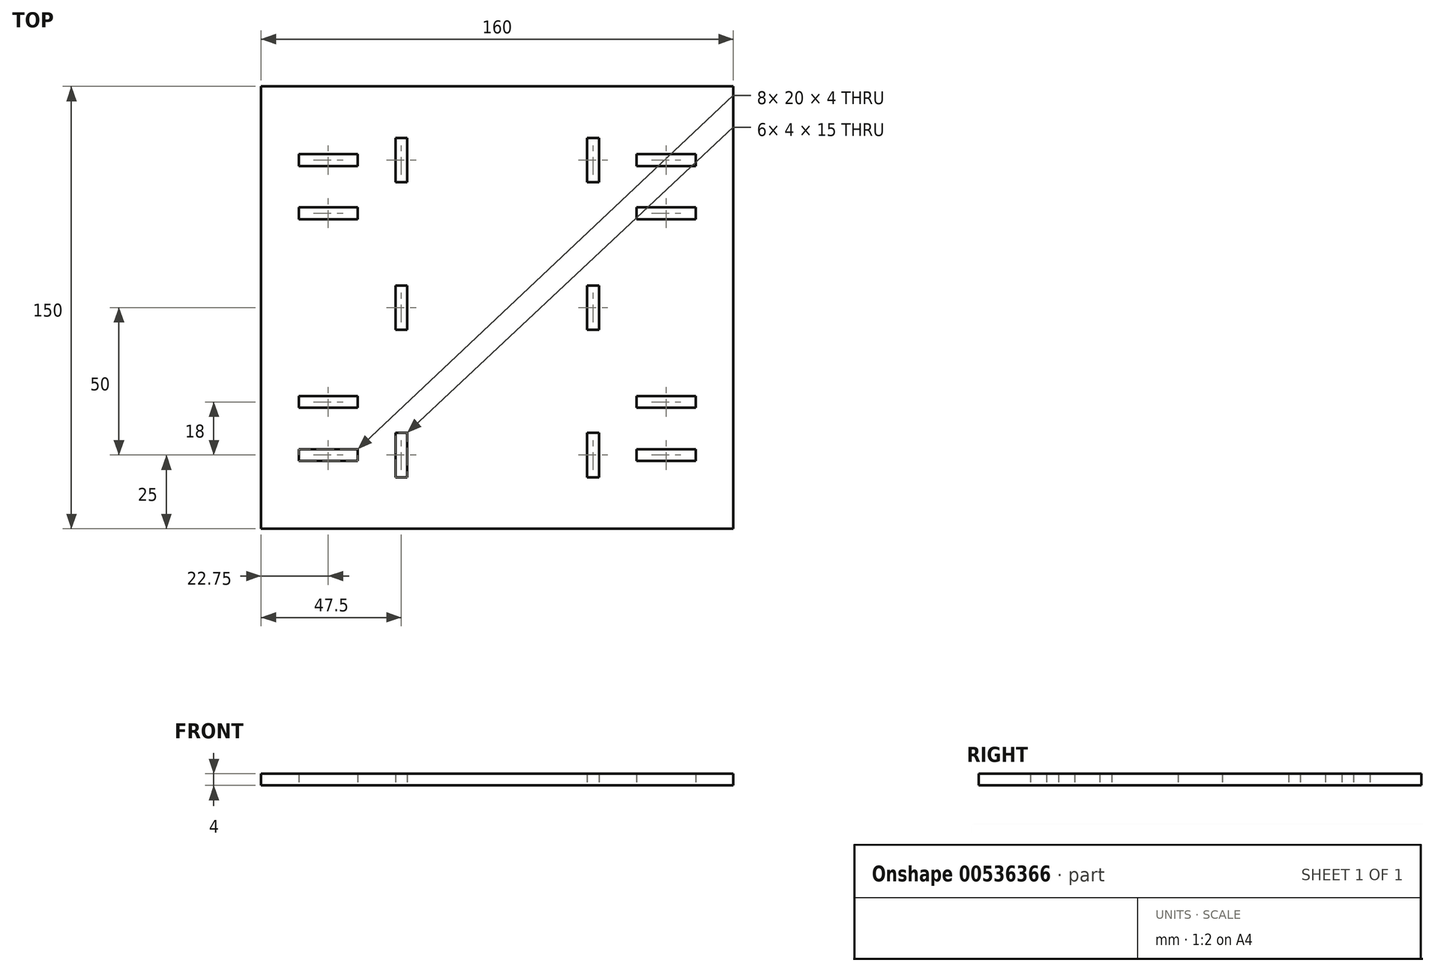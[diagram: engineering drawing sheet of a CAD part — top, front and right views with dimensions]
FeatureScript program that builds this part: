
annotation { "Feature Type Name" : "Feature", "Feature Type Description" : "" }
export const myFeature = defineFeature(function(context is Context, id is Id, definition is map)
    precondition{}
    {
        {
            var Q0;
            Q0=qCreatedBy(makeId("Top.planeOp"),FACE);
            var sketch = newSketch(context, id + "F0", { "sketchPlane" : qUnion([Q0])});
            skLineSegment(sketch, "E0.bottom", {"start": v(-80, 75) * mm, "end": v(80, 75) * mm});
            skLineSegment(sketch, "E0.top", {"start": v(-80, -75) * mm, "end": v(80, -75) * mm});
            skLineSegment(sketch, "E0.left", {"start": v(-80, 75) * mm, "end": v(-80, -75) * mm});
            skLineSegment(sketch, "E0.right", {"start": v(80, 75) * mm, "end": v(80, -75) * mm});
            skPoint(sketch, "E0.middle", {"position": v(0, 0) * mm});
            skLineSegment(sketch, "E1", {"start": v(0, 75) * mm, "end": v(0, -75) * mm});
            skLineSegment(sketch, "E2", {"start": v(0, 0) * mm, "end": v(-30.5, 0) * mm});
            skLineSegment(sketch, "E3", {"start": v(0, 0) * mm, "end": v(30.5, 0) * mm});
            skLineSegment(sketch, "E4", {"start": v(-30.5, 0) * mm, "end": v(-30.5, 7.5) * mm});
            skLineSegment(sketch, "E5", {"start": v(-30.5, 7.5) * mm, "end": v(-30.5, 42.5) * mm});
            skLineSegment(sketch, "E6", {"start": v(-30.5, 42.5) * mm, "end": v(-30.5, 57.5) * mm});
            skPoint(sketch, "E6.endSnap0", {"position": v(-30.5, 25) * mm});
            skLineSegment(sketch, "E7", {"start": v(-30.5, 0) * mm, "end": v(-30.5, -7.5) * mm});
            skLineSegment(sketch, "E8", {"start": v(-30.5, -7.5) * mm, "end": v(-30.5, -42.5) * mm});
            skLineSegment(sketch, "E9", {"start": v(-30.5, -42.5) * mm, "end": v(-30.5, -57.5) * mm});
            skLineSegment(sketch, "E10", {"start": v(-30.5, 57.5) * mm, "end": v(-34.5, 57.5) * mm});
            skLineSegment(sketch, "E11", {"start": v(-34.5, 57.5) * mm, "end": v(-34.5, 42.5) * mm});
            skLineSegment(sketch, "E12", {"start": v(-34.5, 42.5) * mm, "end": v(-30.5, 42.5) * mm});
            skLineSegment(sketch, "E13", {"start": v(-30.5, -57.5) * mm, "end": v(-34.5, -57.5) * mm});
            skLineSegment(sketch, "E14", {"start": v(-34.5, -57.5) * mm, "end": v(-34.5, -42.5) * mm});
            skLineSegment(sketch, "E15", {"start": v(-34.5, -42.5) * mm, "end": v(-30.5, -42.5) * mm});
            skLineSegment(sketch, "E16", {"start": v(30.5, 0) * mm, "end": v(30.5, 7.5) * mm});
            skLineSegment(sketch, "E17", {"start": v(30.5, 7.5) * mm, "end": v(30.5, 42.5) * mm});
            skLineSegment(sketch, "E18", {"start": v(30.5, 42.5) * mm, "end": v(30.5, 57.5) * mm});
            skLineSegment(sketch, "E19", {"start": v(30.5, 57.5) * mm, "end": v(34.5, 57.5) * mm});
            skLineSegment(sketch, "E20", {"start": v(34.5, 57.5) * mm, "end": v(34.5, 42.5) * mm});
            skLineSegment(sketch, "E21", {"start": v(34.5, 42.5) * mm, "end": v(30.5, 42.5) * mm});
            skLineSegment(sketch, "E22", {"start": v(30.5, 0) * mm, "end": v(30.5, -7.5) * mm});
            skLineSegment(sketch, "E23", {"start": v(30.5, -7.5) * mm, "end": v(30.5, -42.5) * mm});
            skLineSegment(sketch, "E24", {"start": v(30.5, -42.5) * mm, "end": v(30.5, -57.5) * mm});
            skLineSegment(sketch, "E25", {"start": v(30.5, -57.5) * mm, "end": v(34.5, -57.5) * mm});
            skLineSegment(sketch, "E26", {"start": v(34.5, -57.5) * mm, "end": v(34.5, -42.5) * mm});
            skLineSegment(sketch, "E27", {"start": v(34.5, -42.5) * mm, "end": v(30.5, -42.5) * mm});
            skLineSegment(sketch, "E28", {"start": v(-30.5, 7.5) * mm, "end": v(-34.5, 7.5) * mm});
            skLineSegment(sketch, "E29", {"start": v(-34.5, 7.5) * mm, "end": v(-34.5, -7.5) * mm});
            skLineSegment(sketch, "E30", {"start": v(-34.5, -7.5) * mm, "end": v(-30.5, -7.5) * mm});
            skLineSegment(sketch, "E31", {"start": v(30.5, 7.5) * mm, "end": v(34.5, 7.5) * mm});
            skLineSegment(sketch, "E32", {"start": v(34.5, 7.5) * mm, "end": v(34.5, -7.5) * mm});
            skLineSegment(sketch, "E33", {"start": v(34.5, -7.5) * mm, "end": v(30.5, -7.5) * mm});
            skSolve(sketch);
        }
        {
            var Q0;
            {var subQ4=sQuery(id+"F0.wireOp",EDGE,"E0.left");Q0=makeQuery(id+"F0.imprint","IMPRINT",FACE,{"disambiguationData":[TD([[makeQuery(id+"F0.imprint","IMPRINT",EDGE,{"derivedFrom":subQ4}),1.0]])]});}
            var Q1;
            {var subQ4=sQuery(id+"F0.wireOp",EDGE,"E0.right");Q1=makeQuery(id+"F0.imprint","IMPRINT",FACE,{"disambiguationData":[TD([[makeQuery(id+"F0.imprint","IMPRINT",EDGE,{"derivedFrom":subQ4}),-1.0]])]});}
            extrude(context, id + "F1", {"entities" : qUnion([Q0, Q1]), "depth" : 4 * mm, "offsetDistance" : 25 * mm});
        }
        {
            var Q0;
            Q0=makeQuery(id+"F1.opExtrude","CAP_FACE",FACE,{"disambiguationData":[OSD([sQuery(id+"F0.wireOp",EDGE,"E0.bottom"),sQuery(id+"F0.wireOp",EDGE,"E0.top"),sQuery(id+"F0.wireOp",EDGE,"E0.left"),sQuery(id+"F0.wireOp",EDGE,"E0.right"),sQuery(id+"F0.wireOp",EDGE,"E4"),sQuery(id+"F0.wireOp",EDGE,"E6"),sQuery(id+"F0.wireOp",EDGE,"E7"),sQuery(id+"F0.wireOp",EDGE,"E9"),sQuery(id+"F0.wireOp",EDGE,"E10"),sQuery(id+"F0.wireOp",EDGE,"E11"),sQuery(id+"F0.wireOp",EDGE,"E12"),sQuery(id+"F0.wireOp",EDGE,"E13"),sQuery(id+"F0.wireOp",EDGE,"E14"),sQuery(id+"F0.wireOp",EDGE,"E15"),sQuery(id+"F0.wireOp",EDGE,"E16"),sQuery(id+"F0.wireOp",EDGE,"E18"),sQuery(id+"F0.wireOp",EDGE,"E19"),sQuery(id+"F0.wireOp",EDGE,"E20"),sQuery(id+"F0.wireOp",EDGE,"E21"),sQuery(id+"F0.wireOp",EDGE,"E22"),sQuery(id+"F0.wireOp",EDGE,"E24"),sQuery(id+"F0.wireOp",EDGE,"E25"),sQuery(id+"F0.wireOp",EDGE,"E26"),sQuery(id+"F0.wireOp",EDGE,"E27"),sQuery(id+"F0.wireOp",EDGE,"E28"),sQuery(id+"F0.wireOp",EDGE,"E29"),sQuery(id+"F0.wireOp",EDGE,"E30"),sQuery(id+"F0.wireOp",EDGE,"E31"),sQuery(id+"F0.wireOp",EDGE,"E32"),sQuery(id+"F0.wireOp",EDGE,"E33")])],"isStart":true});
            var sketch = newSketch(context, id + "F2", { "sketchPlane" : qUnion([Q0])});
            skLineSegment(sketch, "E34", {"start": v(-34.5, 50) * mm, "end": v(-80, 50) * mm});
            skLineSegment(sketch, "E35.bottom", {"start": v(-47.25, 52) * mm, "end": v(-67.25, 52) * mm});
            skLineSegment(sketch, "E35.top", {"start": v(-47.25, 48) * mm, "end": v(-67.25, 48) * mm});
            skLineSegment(sketch, "E35.left", {"start": v(-47.25, 52) * mm, "end": v(-47.25, 48) * mm});
            skLineSegment(sketch, "E35.right", {"start": v(-67.25, 52) * mm, "end": v(-67.25, 48) * mm});
            skPoint(sketch, "E35.middle", {"position": v(-57.25, 50) * mm});
            skLineSegment(sketch, "E36", {"start": v(-57.25, 52) * mm, "end": v(-57.25, 32) * mm});
            skPoint(sketch, "E36.endSnap0", {"position": v(-57.25, 48) * mm});
            skLineSegment(sketch, "E37.bottom", {"start": v(-47.25, 30) * mm, "end": v(-67.25, 30) * mm});
            skLineSegment(sketch, "E37.top", {"start": v(-47.25, 34) * mm, "end": v(-67.25, 34) * mm});
            skLineSegment(sketch, "E37.left", {"start": v(-47.25, 30) * mm, "end": v(-47.25, 34) * mm});
            skLineSegment(sketch, "E37.right", {"start": v(-67.25, 30) * mm, "end": v(-67.25, 34) * mm});
            skPoint(sketch, "E37.middle", {"position": v(-57.25, 32) * mm});
            skLineSegment(sketch, "E38", {"start": v(34.5, 50) * mm, "end": v(80, 50) * mm});
            skLineSegment(sketch, "E39.bottom", {"start": v(67.25, 48) * mm, "end": v(47.25, 48) * mm});
            skLineSegment(sketch, "E39.top", {"start": v(67.25, 52) * mm, "end": v(47.25, 52) * mm});
            skLineSegment(sketch, "E39.left", {"start": v(67.25, 48) * mm, "end": v(67.25, 52) * mm});
            skLineSegment(sketch, "E39.right", {"start": v(47.25, 48) * mm, "end": v(47.25, 52) * mm});
            skPoint(sketch, "E39.middle", {"position": v(57.25, 50) * mm});
            skLineSegment(sketch, "E40", {"start": v(57.25, 52) * mm, "end": v(57.25, 32) * mm});
            skLineSegment(sketch, "E41.bottom", {"start": v(47.25, 34) * mm, "end": v(67.25, 34) * mm});
            skLineSegment(sketch, "E41.top", {"start": v(47.25, 30) * mm, "end": v(67.25, 30) * mm});
            skLineSegment(sketch, "E41.left", {"start": v(47.25, 34) * mm, "end": v(47.25, 30) * mm});
            skLineSegment(sketch, "E41.right", {"start": v(67.25, 34) * mm, "end": v(67.25, 30) * mm});
            skPoint(sketch, "E41.middle", {"position": v(57.25, 32) * mm});
            skLineSegment(sketch, "E42", {"start": v(34.5, -50) * mm, "end": v(80, -50) * mm});
            skLineSegment(sketch, "E43.bottom", {"start": v(67.25, -52) * mm, "end": v(47.25, -52) * mm});
            skLineSegment(sketch, "E43.top", {"start": v(67.25, -48) * mm, "end": v(47.25, -48) * mm});
            skLineSegment(sketch, "E43.left", {"start": v(67.25, -52) * mm, "end": v(67.25, -48) * mm});
            skLineSegment(sketch, "E43.right", {"start": v(47.25, -52) * mm, "end": v(47.25, -48) * mm});
            skPoint(sketch, "E43.middle", {"position": v(57.25, -50) * mm});
            skLineSegment(sketch, "E44", {"start": v(57.25, -52) * mm, "end": v(57.25, -32) * mm});
            skLineSegment(sketch, "E45.bottom", {"start": v(47.25, -34) * mm, "end": v(67.25, -34) * mm});
            skLineSegment(sketch, "E45.top", {"start": v(47.25, -30) * mm, "end": v(67.25, -30) * mm});
            skLineSegment(sketch, "E45.left", {"start": v(47.25, -34) * mm, "end": v(47.25, -30) * mm});
            skLineSegment(sketch, "E45.right", {"start": v(67.25, -34) * mm, "end": v(67.25, -30) * mm});
            skPoint(sketch, "E45.middle", {"position": v(57.25, -32) * mm});
            skLineSegment(sketch, "E46", {"start": v(-34.5, -50) * mm, "end": v(-80, -50) * mm});
            skLineSegment(sketch, "E47.bottom", {"start": v(-47.25, -48) * mm, "end": v(-67.25, -48) * mm});
            skLineSegment(sketch, "E47.top", {"start": v(-47.25, -52) * mm, "end": v(-67.25, -52) * mm});
            skLineSegment(sketch, "E47.left", {"start": v(-47.25, -48) * mm, "end": v(-47.25, -52) * mm});
            skLineSegment(sketch, "E47.right", {"start": v(-67.25, -48) * mm, "end": v(-67.25, -52) * mm});
            skPoint(sketch, "E47.middle", {"position": v(-57.25, -50) * mm});
            skLineSegment(sketch, "E48", {"start": v(-57.25, -52) * mm, "end": v(-57.25, -32) * mm});
            skPoint(sketch, "E48.endSnap0", {"position": v(-57.25, -48) * mm});
            skLineSegment(sketch, "E49.bottom", {"start": v(-47.25, -34) * mm, "end": v(-67.25, -34) * mm});
            skLineSegment(sketch, "E49.top", {"start": v(-47.25, -30) * mm, "end": v(-67.25, -30) * mm});
            skLineSegment(sketch, "E49.left", {"start": v(-47.25, -34) * mm, "end": v(-47.25, -30) * mm});
            skLineSegment(sketch, "E49.right", {"start": v(-67.25, -34) * mm, "end": v(-67.25, -30) * mm});
            skPoint(sketch, "E49.middle", {"position": v(-57.25, -32) * mm});
            skSolve(sketch);
        }
        {
            var Q0;
            Q0=makeQuery(id+"F2.imprint","IMPRINT",FACE,{"disambiguationData":[TD([[makeQuery(id+"F2.imprint","IMPRINT",EDGE,{"derivedFrom":sQuery(id+"F2.wireOp",EDGE,"E37.bottom")}),-1.0]])]});
            var Q1;
            Q1=makeQuery(id+"F2.imprint","IMPRINT",FACE,{"disambiguationData":[TD([[makeQuery(id+"F2.imprint","IMPRINT",EDGE,{"derivedFrom":sQuery(id+"F2.wireOp",EDGE,"E41.top")}),1.0]])]});
            var Q2;
            {var subQ0=sQuery(id+"F2.wireOp",EDGE,"E39.left");var subQ1=sQuery(id+"F2.wireOp",EDGE,"E38");var subQ2=makeQuery(id+"F2.imprint","INTERSECT",VERTEX,{"derivedFrom":[subQ1,subQ0]});Q2=makeQuery(id+"F2.imprint","IMPRINT",FACE,{"disambiguationData":[TD([[makeQuery(id+"F2.imprint","IMPRINT",EDGE,{"disambiguationData":[TD([[subQ2,1.0]])],"derivedFrom":subQ1}),1.0]])]});}
            var Q3;
            {var subQ0=sQuery(id+"F2.wireOp",EDGE,"E39.right");var subQ1=sQuery(id+"F2.wireOp",EDGE,"E38");var subQ2=makeQuery(id+"F2.imprint","INTERSECT",VERTEX,{"derivedFrom":[subQ1,subQ0]});Q3=makeQuery(id+"F2.imprint","IMPRINT",FACE,{"disambiguationData":[TD([[makeQuery(id+"F2.imprint","IMPRINT",EDGE,{"disambiguationData":[TD([[subQ2,-1.0]])],"derivedFrom":subQ1}),1.0]])]});}
            var Q4;
            {var subQ0=sQuery(id+"F2.wireOp",EDGE,"E39.left");var subQ1=sQuery(id+"F2.wireOp",EDGE,"E38");var subQ2=makeQuery(id+"F2.imprint","INTERSECT",VERTEX,{"derivedFrom":[subQ1,subQ0]});Q4=makeQuery(id+"F2.imprint","IMPRINT",FACE,{"disambiguationData":[TD([[makeQuery(id+"F2.imprint","IMPRINT",EDGE,{"disambiguationData":[TD([[subQ2,1.0]])],"derivedFrom":subQ1}),-1.0]])]});}
            var Q5;
            {var subQ0=sQuery(id+"F2.wireOp",EDGE,"E39.right");var subQ1=sQuery(id+"F2.wireOp",EDGE,"E38");var subQ2=makeQuery(id+"F2.imprint","INTERSECT",VERTEX,{"derivedFrom":[subQ1,subQ0]});Q5=makeQuery(id+"F2.imprint","IMPRINT",FACE,{"disambiguationData":[TD([[makeQuery(id+"F2.imprint","IMPRINT",EDGE,{"disambiguationData":[TD([[subQ2,-1.0]])],"derivedFrom":subQ1}),-1.0]])]});}
            var Q6;
            {var subQ0=sQuery(id+"F2.wireOp",EDGE,"E35.left");var subQ1=sQuery(id+"F2.wireOp",EDGE,"E34");var subQ2=makeQuery(id+"F2.imprint","INTERSECT",VERTEX,{"derivedFrom":[subQ1,subQ0]});Q6=makeQuery(id+"F2.imprint","IMPRINT",FACE,{"disambiguationData":[TD([[makeQuery(id+"F2.imprint","IMPRINT",EDGE,{"disambiguationData":[TD([[subQ2,-1.0]])],"derivedFrom":subQ1}),-1.0]])]});}
            var Q7;
            {var subQ0=sQuery(id+"F2.wireOp",EDGE,"E35.right");var subQ1=sQuery(id+"F2.wireOp",EDGE,"E34");var subQ2=makeQuery(id+"F2.imprint","INTERSECT",VERTEX,{"derivedFrom":[subQ1,subQ0]});Q7=makeQuery(id+"F2.imprint","IMPRINT",FACE,{"disambiguationData":[TD([[makeQuery(id+"F2.imprint","IMPRINT",EDGE,{"disambiguationData":[TD([[subQ2,1.0]])],"derivedFrom":subQ1}),-1.0]])]});}
            var Q8;
            {var subQ0=sQuery(id+"F2.wireOp",EDGE,"E35.left");var subQ1=sQuery(id+"F2.wireOp",EDGE,"E34");var subQ2=makeQuery(id+"F2.imprint","INTERSECT",VERTEX,{"derivedFrom":[subQ1,subQ0]});Q8=makeQuery(id+"F2.imprint","IMPRINT",FACE,{"disambiguationData":[TD([[makeQuery(id+"F2.imprint","IMPRINT",EDGE,{"disambiguationData":[TD([[subQ2,-1.0]])],"derivedFrom":subQ1}),1.0]])]});}
            var Q9;
            {var subQ0=sQuery(id+"F2.wireOp",EDGE,"E35.right");var subQ1=sQuery(id+"F2.wireOp",EDGE,"E34");var subQ2=makeQuery(id+"F2.imprint","INTERSECT",VERTEX,{"derivedFrom":[subQ1,subQ0]});Q9=makeQuery(id+"F2.imprint","IMPRINT",FACE,{"disambiguationData":[TD([[makeQuery(id+"F2.imprint","IMPRINT",EDGE,{"disambiguationData":[TD([[subQ2,1.0]])],"derivedFrom":subQ1}),1.0]])]});}
            var Q10;
            Q10=makeQuery(id+"F2.imprint","IMPRINT",FACE,{"disambiguationData":[TD([[makeQuery(id+"F2.imprint","IMPRINT",EDGE,{"derivedFrom":sQuery(id+"F2.wireOp",EDGE,"E45.top")}),-1.0]])]});
            var Q11;
            {var subQ0=sQuery(id+"F2.wireOp",EDGE,"E43.right");var subQ1=sQuery(id+"F2.wireOp",EDGE,"E42");var subQ2=makeQuery(id+"F2.imprint","INTERSECT",VERTEX,{"derivedFrom":[subQ1,subQ0]});Q11=makeQuery(id+"F2.imprint","IMPRINT",FACE,{"disambiguationData":[TD([[makeQuery(id+"F2.imprint","IMPRINT",EDGE,{"disambiguationData":[TD([[subQ2,-1.0]])],"derivedFrom":subQ1}),1.0]])]});}
            var Q12;
            {var subQ0=sQuery(id+"F2.wireOp",EDGE,"E43.left");var subQ1=sQuery(id+"F2.wireOp",EDGE,"E42");var subQ2=makeQuery(id+"F2.imprint","INTERSECT",VERTEX,{"derivedFrom":[subQ1,subQ0]});Q12=makeQuery(id+"F2.imprint","IMPRINT",FACE,{"disambiguationData":[TD([[makeQuery(id+"F2.imprint","IMPRINT",EDGE,{"disambiguationData":[TD([[subQ2,1.0]])],"derivedFrom":subQ1}),1.0]])]});}
            var Q13;
            {var subQ0=sQuery(id+"F2.wireOp",EDGE,"E43.left");var subQ1=sQuery(id+"F2.wireOp",EDGE,"E42");var subQ2=makeQuery(id+"F2.imprint","INTERSECT",VERTEX,{"derivedFrom":[subQ1,subQ0]});Q13=makeQuery(id+"F2.imprint","IMPRINT",FACE,{"disambiguationData":[TD([[makeQuery(id+"F2.imprint","IMPRINT",EDGE,{"disambiguationData":[TD([[subQ2,1.0]])],"derivedFrom":subQ1}),-1.0]])]});}
            var Q14;
            {var subQ0=sQuery(id+"F2.wireOp",EDGE,"E43.right");var subQ1=sQuery(id+"F2.wireOp",EDGE,"E42");var subQ2=makeQuery(id+"F2.imprint","INTERSECT",VERTEX,{"derivedFrom":[subQ1,subQ0]});Q14=makeQuery(id+"F2.imprint","IMPRINT",FACE,{"disambiguationData":[TD([[makeQuery(id+"F2.imprint","IMPRINT",EDGE,{"disambiguationData":[TD([[subQ2,-1.0]])],"derivedFrom":subQ1}),-1.0]])]});}
            var Q15;
            Q15=makeQuery(id+"F2.imprint","IMPRINT",FACE,{"disambiguationData":[TD([[makeQuery(id+"F2.imprint","IMPRINT",EDGE,{"derivedFrom":sQuery(id+"F2.wireOp",EDGE,"E49.top")}),1.0]])]});
            var Q16;
            {var subQ0=sQuery(id+"F2.wireOp",EDGE,"E47.left");var subQ1=sQuery(id+"F2.wireOp",EDGE,"E46");var subQ2=makeQuery(id+"F2.imprint","INTERSECT",VERTEX,{"derivedFrom":[subQ1,subQ0]});Q16=makeQuery(id+"F2.imprint","IMPRINT",FACE,{"disambiguationData":[TD([[makeQuery(id+"F2.imprint","IMPRINT",EDGE,{"disambiguationData":[TD([[subQ2,-1.0]])],"derivedFrom":subQ1}),-1.0]])]});}
            var Q17;
            {var subQ0=sQuery(id+"F2.wireOp",EDGE,"E47.left");var subQ1=sQuery(id+"F2.wireOp",EDGE,"E46");var subQ2=makeQuery(id+"F2.imprint","INTERSECT",VERTEX,{"derivedFrom":[subQ1,subQ0]});Q17=makeQuery(id+"F2.imprint","IMPRINT",FACE,{"disambiguationData":[TD([[makeQuery(id+"F2.imprint","IMPRINT",EDGE,{"disambiguationData":[TD([[subQ2,-1.0]])],"derivedFrom":subQ1}),1.0]])]});}
            var Q18;
            {var subQ0=sQuery(id+"F2.wireOp",EDGE,"E47.right");var subQ1=sQuery(id+"F2.wireOp",EDGE,"E46");var subQ2=makeQuery(id+"F2.imprint","INTERSECT",VERTEX,{"derivedFrom":[subQ1,subQ0]});Q18=makeQuery(id+"F2.imprint","IMPRINT",FACE,{"disambiguationData":[TD([[makeQuery(id+"F2.imprint","IMPRINT",EDGE,{"disambiguationData":[TD([[subQ2,1.0]])],"derivedFrom":subQ1}),-1.0]])]});}
            var Q19;
            {var subQ0=sQuery(id+"F2.wireOp",EDGE,"E47.right");var subQ1=sQuery(id+"F2.wireOp",EDGE,"E46");var subQ2=makeQuery(id+"F2.imprint","INTERSECT",VERTEX,{"derivedFrom":[subQ1,subQ0]});Q19=makeQuery(id+"F2.imprint","IMPRINT",FACE,{"disambiguationData":[TD([[makeQuery(id+"F2.imprint","IMPRINT",EDGE,{"disambiguationData":[TD([[subQ2,1.0]])],"derivedFrom":subQ1}),1.0]])]});}
            extrude(context, id + "F3", {"entities" : qUnion([Q0, Q1, Q2, Q3, Q4, Q5, Q6, Q7, Q8, Q9, Q10, Q11, Q12, Q13, Q14, Q15, Q16, Q17, Q18, Q19]), "operationType" : NewBodyOperationType.REMOVE, "oppositeDirection" : true, "depth" : 25 * mm, "offsetDistance" : 25 * mm});
        }
    });
